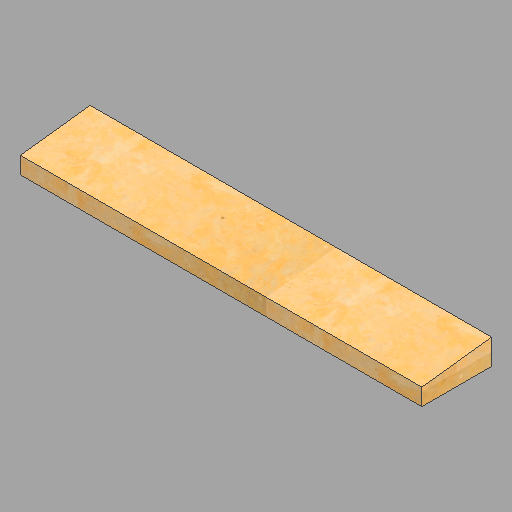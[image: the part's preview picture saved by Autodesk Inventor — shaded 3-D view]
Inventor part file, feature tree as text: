
AUTODESK INVENTOR PART (.ipt)
format: ipt  version: 2023 (Build 270158030, 158C)  size: 192,000 bytes
history: native  units: in
note: dims shown in document units (in); Inventor stores cm internally (conversion verified against a paired STEP export)
features: extrude x1, sketch x1
ambient origin geometry x8: Origin, YZ Plane, XZ Plane, XY Plane, X Axis, Y Axis, Z Axis, Center Point
bodies: Solid1 (feature_tree)
feature tree (2):
  extrude  "Extrusion1"  Depth=8.25in
  sketch  "Sketch1"  dims[d0=3.0in d1=8.25in d2=2.0in d3=47.5in d4=0.0in]
